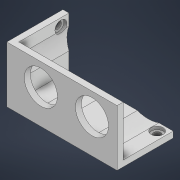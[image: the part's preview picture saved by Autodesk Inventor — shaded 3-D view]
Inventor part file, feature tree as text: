
AUTODESK INVENTOR PART (.ipt)
format: ipt  version: 2022 (Build 260153000, 153)  size: 162,304 bytes
history: native  units: mm
features: sketch x5, extrude x3, hole x2, projected_geometry x1
ambient origin geometry x8: Origin, YZ Plane, XZ Plane, XY Plane, X Axis, Y Axis, Z Axis, Center Point
bodies: Volumenkörper1 (feature_tree)
feature tree (11):
  extrude  "Extrusion1"  Depth=17.0mm
  extrude  "Extrusion2"  Depth=3.0mm TaperAngle=0.0deg
  hole  "Bohrung1"  [1 undecoded]
  hole  "Bohrung2"  [1 undecoded]
  extrude  "Extrusion3"  Depth=4.0mm
  sketch  "Skizze1"  dims[d1=16.5mm d5=17.0mm]
  sketch  "Skizze2"  dims[d7=11.0mm d8=3.0mm d9=0.0mm]
  projected_geometry  "Projizierte Kontur1"
  sketch  "Skizze3"  dims[d11=3.0mm d12=25.0mm d13=0.0mm]
  sketch  "Skizze4"  dims[d14=12.5mm]
  sketch  "Skizze5"  dims[d15=3.5mm d16=6.0mm d17=6.0mm d18=1.5mm d19=90.0deg d20=8.0mm d21=20.594885mm d22=4.0mm d23=4.0mm d24=3.5mm d25=6.0mm d26=6.0mm d27=1.5mm d28=90.0deg d29=8.0mm d30=20.594885mm d31=4.0mm d32=4.0mm d33=30.0mm d34=30.0mm d35=25.0mm d36=0.0mm]
note: 2 required parameter values undecoded (feature->parameter linkage not recoverable at this tier; creation-order binding heuristic only, values carry confidence <= 0.55)
